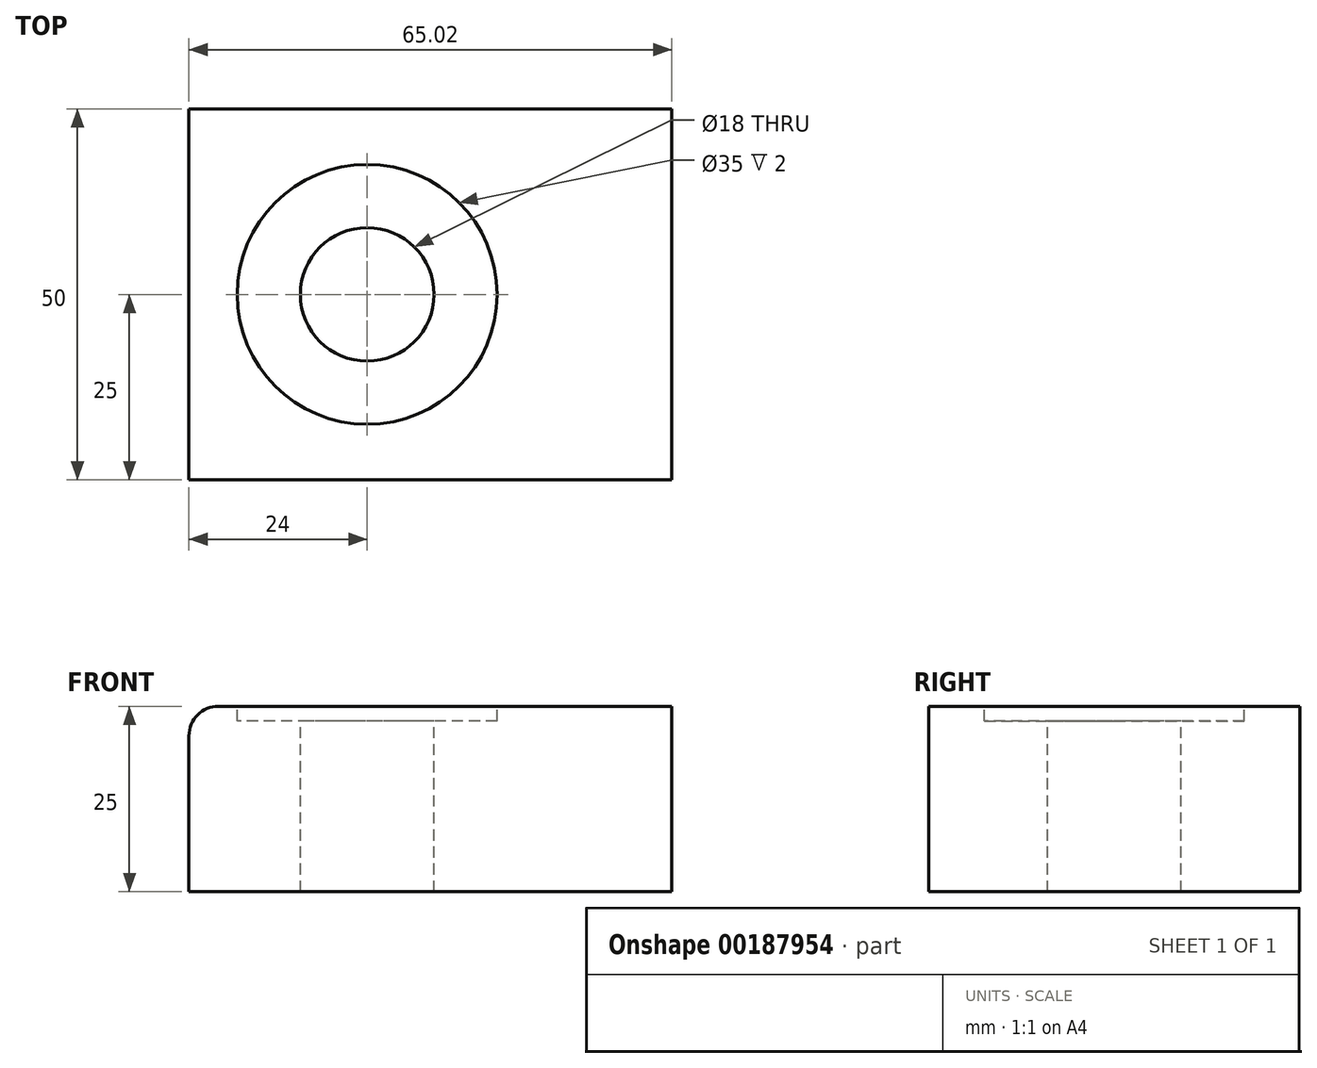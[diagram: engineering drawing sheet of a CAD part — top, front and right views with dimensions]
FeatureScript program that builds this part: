
annotation { "Feature Type Name" : "Feature", "Feature Type Description" : "" }
export const myFeature = defineFeature(function(context is Context, id is Id, definition is map)
    precondition{}
    {
        {
            var Q0;
            Q0=qCreatedBy(makeId("Top.planeOp"),FACE);
            var sketch = newSketch(context, id + "F0", { "sketchPlane" : qUnion([Q0])});
            skLineSegment(sketch, "E0.bottom", {"start": v(-24, 25) * mm, "end": v(41.02, 25) * mm});
            skLineSegment(sketch, "E0.top", {"start": v(-24, -25) * mm, "end": v(41.02, -25) * mm});
            skLineSegment(sketch, "E0.left", {"start": v(-24, 25) * mm, "end": v(-24, -25) * mm});
            skLineSegment(sketch, "E0.right", {"start": v(41.02, 25) * mm, "end": v(41.02, -25) * mm});
            skSolve(sketch);
        }
        {
            var Q0;
            Q0 = qSketchRegion(id + "F0", true);
            extrude(context, id + "F1", {"entities" : qUnion([Q0]), "oppositeDirection" : true, "depth" : 25 * mm});
        }
        {
            var Q0;
            Q0=makeQuery(id+"F1.opExtrude","CAP_FACE",FACE,{"disambiguationData":[OSD([sQuery(id+"F0.wireOp",EDGE,"E0.bottom"),sQuery(id+"F0.wireOp",EDGE,"E0.top"),sQuery(id+"F0.wireOp",EDGE,"E0.left"),sQuery(id+"F0.wireOp",EDGE,"E0.right")])],"isStart":true});
            var sketch = newSketch(context, id + "F2", { "sketchPlane" : qUnion([Q0])});
            skCircle(sketch, "E1", {"center": v(0, 0) * mm, "radius": 9 * mm});
            skSolve(sketch);
        }
        {
            var Q0;
            Q0 = qSketchRegion(id + "F2", true);
            extrude(context, id + "F3", {"entities" : qUnion([Q0]), "operationType" : NewBodyOperationType.REMOVE, "endBound" : BoundingType.THROUGH_ALL, "oppositeDirection" : true, "depth" : 25 * mm});
        }
        {
            var Q0;
            Q0=makeQuery(id+"F1.opExtrude","CAP_FACE",FACE,{"disambiguationData":[OSD([sQuery(id+"F0.wireOp",EDGE,"E0.bottom"),sQuery(id+"F0.wireOp",EDGE,"E0.top"),sQuery(id+"F0.wireOp",EDGE,"E0.left"),sQuery(id+"F0.wireOp",EDGE,"E0.right")])],"isStart":true});
            var sketch = newSketch(context, id + "F4", { "sketchPlane" : qUnion([Q0])});
            skCircle(sketch, "E2", {"center": v(0, 0) * mm, "radius": 17.5 * mm});
            skSolve(sketch);
        }
        {
            var Q0;
            Q0 = qSketchRegion(id + "F4", true);
            extrude(context, id + "F5", {"entities" : qUnion([Q0]), "operationType" : NewBodyOperationType.REMOVE, "oppositeDirection" : true, "depth" : 2 * mm});
        }
        {
            var Q0;
            Q0=makeQuery(id+"F1.opExtrude","CAP_EDGE",EDGE,{"disambiguationData":[OSD([sQuery(id+"F0.wireOp",EDGE,"E0.left")])],"isStart":true});
            fillet(context, id + "F6", {"entities" : qUnion([Q0]), "radius" : 4 * mm, "tangentPropagation" : true, "allowEdgeOverflow" : false});
        }
    });
